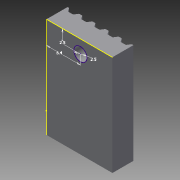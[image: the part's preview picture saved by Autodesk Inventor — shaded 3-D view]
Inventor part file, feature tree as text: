
AUTODESK INVENTOR PART (.ipt)
format: ipt  version: 2015 SP1 (Build 190203100, 203)  size: 176,128 bytes
history: native  units: in
note: dims shown in document units (in); Inventor stores cm internally (conversion verified against a paired STEP export)
features: sketch x5, extrude x4, projected_geometry x1
ambient origin geometry x8: Origin, YZ Plane, XZ Plane, XY Plane, X Axis, Y Axis, Z Axis, Center Point
bodies: Body1 (feature_tree)
feature tree (10):
  extrude  "Extrusion2"  Depth=0.1575in TaperAngle=0.0deg
  extrude  "Extrusion3"  Depth=0.0079in
  extrude  "Extrusion4"  Depth=0.3937in
  sketch  "Sketch5"  dims[d20=0.0984in d21=0.0984in]
  sketch  "Sketch6"  dims[d22=0.252in d23=0.3937in d24=0.0in]
  extrude  "Extrusion5"  Depth=0.0984in
  sketch  "Sketch1"  dims[d2=0.1575in d3=0.0in d4=0.1575in d5=0.0in]
  sketch  "Sketch2"  dims[d11=0.0118in d12=0.0079in d13=0.0079in d14=0.0984in d16=0.0394in]
  projected_geometry  "Projected Loop1"
  sketch  "Sketch4"  dims[d17=0.3937in d18=0.0in d19=0.0984in]
